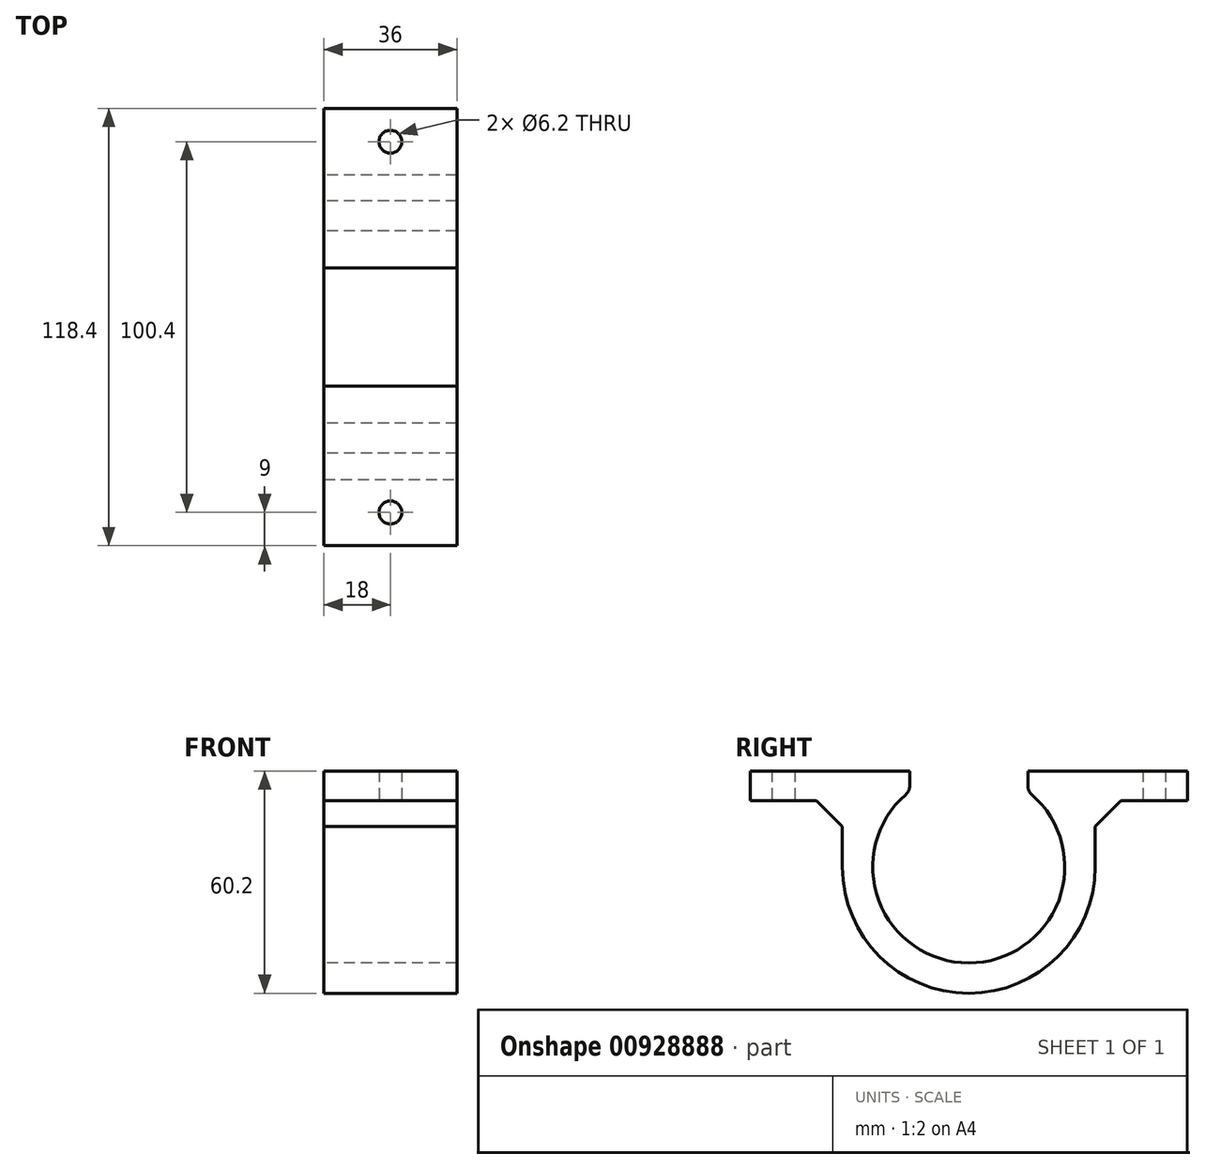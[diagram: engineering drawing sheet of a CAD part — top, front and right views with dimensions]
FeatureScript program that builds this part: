
annotation { "Feature Type Name" : "Feature", "Feature Type Description" : "" }
export const myFeature = defineFeature(function(context is Context, id is Id, definition is map)
    precondition{}
    {
        {
            var Q0;
            Q0=qCreatedBy(makeId("Right.planeOp"),FACE);
            var sketch = newSketch(context, id + "F0", { "sketchPlane" : qUnion([Q0])});
            skCircle(sketch, "E0", {"center": v(0, 0) * mm, "radius": 26 * mm, "construction": true});
            skLineSegment(sketch, "E1", {"start": v(26, 0) * mm, "end": v(26, 26) * mm, "construction": true});
            skLineSegment(sketch, "E2", {"start": v(26, 26) * mm, "end": v(-26, 26) * mm, "construction": true});
            skLineSegment(sketch, "E3", {"start": v(-26, 26) * mm, "end": v(-26, 0) * mm, "construction": true});
            skLineSegment(sketch, "E4", {"start": v(-26, 0) * mm, "end": v(26, 0) * mm, "construction": true});
            skLineSegment(sketch, "E5", {"start": v(-26, 26) * mm, "end": v(-59.2, 26) * mm});
            skLineSegment(sketch, "E6", {"start": v(-59.2, 26) * mm, "end": v(-59.2, 18) * mm});
            skLineSegment(sketch, "E7", {"start": v(-59.2, 18) * mm, "end": v(-34.2, 18) * mm});
            skLineSegment(sketch, "E8", {"start": v(-34.2, 18) * mm, "end": v(-34.2, 0) * mm});
            skLineSegment(sketch, "E9", {"start": v(26, 26) * mm, "end": v(59.2, 26) * mm});
            skLineSegment(sketch, "E10", {"start": v(59.2, 26) * mm, "end": v(59.2, 18) * mm});
            skLineSegment(sketch, "E11", {"start": v(59.2, 18) * mm, "end": v(34.2, 18) * mm});
            skLineSegment(sketch, "E12", {"start": v(34.2, 18) * mm, "end": v(34.2, 0) * mm});
            skArc(sketch, "E13", {"start": v(-34.2, 0) * mm, "mid": v(0, -34.2) * mm, "end": v(34.2, 0) * mm});
            skArc(sketch, "E14", {"start": v(-26, 0) * mm, "mid": v(0, -26) * mm, "end": v(26, 0) * mm});
            skLineSegment(sketch, "E15", {"start": v(-46.7, 18) * mm, "end": v(-46.7, 26) * mm, "construction": true});
            skLineSegment(sketch, "E16", {"start": v(46.7, 18) * mm, "end": v(46.7, 26) * mm, "construction": true});
            skLineSegment(sketch, "E17", {"start": v(34.2, 18) * mm, "end": v(34.2, 26) * mm, "construction": true});
            skLineSegment(sketch, "E18", {"start": v(-34.2, 18) * mm, "end": v(-34.2, 26) * mm, "construction": true});
            skArc(sketch, "E19", {"start": v(26, 0) * mm, "mid": v(23.37, 11.4) * mm, "end": v(16, 20.5) * mm});
            skLineSegment(sketch, "E20", {"start": v(26, 26) * mm, "end": v(16, 26) * mm});
            skLineSegment(sketch, "E21", {"start": v(16, 26) * mm, "end": v(16, 20.5) * mm});
            skArc(sketch, "E22", {"start": v(-26, 0) * mm, "mid": v(-23.37, 11.4) * mm, "end": v(-16, 20.5) * mm});
            skLineSegment(sketch, "E23", {"start": v(16, 20.5) * mm, "end": v(-16, 20.5) * mm, "construction": true});
            skLineSegment(sketch, "E24", {"start": v(-16, 20.5) * mm, "end": v(-16, 26) * mm});
            skLineSegment(sketch, "E25", {"start": v(-16, 26) * mm, "end": v(-26, 26) * mm});
            skSolve(sketch);
        }
        {
            var Q0;
            Q0=makeQuery(id+"F0.imprint","IMPRINT",FACE,{"disambiguationData":[TD([[makeQuery(id+"F0.imprint","IMPRINT",EDGE,{"derivedFrom":sQuery(id+"F0.wireOp",EDGE,"E5")}),1.0]])]});
            extrude(context, id + "F1", {"entities" : qUnion([Q0]), "depth" : 36 * mm, "offsetDistance" : 25 * mm});
        }
        {
            var Q0;
            Q0=makeQuery(id+"F1.opExtrude","SWEPT_FACE",FACE,{"disambiguationData":[OSD([sQuery(id+"F0.wireOp",EDGE,"E7")])]});
            var sketch = newSketch(context, id + "F2", { "sketchPlane" : qUnion([Q0])});
            skLineSegment(sketch, "E26", {"start": v(36, 50.2) * mm, "end": v(0, 50.2) * mm, "construction": true});
            skCircle(sketch, "E27", {"center": v(18, 50.2) * mm, "radius": 3.1 * mm});
            skLineSegment(sketch, "E28", {"start": v(36, -50.2) * mm, "end": v(0, -50.2) * mm, "construction": true});
            skCircle(sketch, "E29", {"center": v(18, -50.2) * mm, "radius": 3.1 * mm});
            skCircle(sketch, "E30", {"center": v(18, 50.2) * mm, "radius": 9 * mm, "construction": true});
            skCircle(sketch, "E31", {"center": v(18, -50.2) * mm, "radius": 9 * mm, "construction": true});
            skSolve(sketch);
        }
        {
            var Q0;
            Q0=qSketchRegion(id+"F2",true);
            extrude(context, id + "F3", {"entities" : qUnion([Q0]), "operationType" : NewBodyOperationType.REMOVE, "endBound" : BoundingType.THROUGH_ALL, "oppositeDirection" : true, "depth" : 25 * mm, "offsetDistance" : 25 * mm});
        }
        {
            var Q0;
            Q0=makeQuery(id+"F1.opExtrude","SWEPT_EDGE",EDGE,{"disambiguationData":[OSD([sQuery(id+"F0.wireOp",EDGE,"E7"),sQuery(id+"F0.wireOp",EDGE,"E8")])]});
            var Q1;
            Q1=makeQuery(id+"F1.opExtrude","SWEPT_EDGE",EDGE,{"disambiguationData":[OSD([sQuery(id+"F0.wireOp",EDGE,"E11"),sQuery(id+"F0.wireOp",EDGE,"E12")])]});
            chamfer(context, id + "F4", {"entities" : qUnion([Q0, Q1]), "width" : 7 * mm, "tangentPropagation" : true});
        }
        {
            var Q0;
            Q0=makeQuery(id+"F1.opExtrude","SWEPT_EDGE",EDGE,{"disambiguationData":[OSD([sQuery(id+"F0.wireOp",EDGE,"E19"),sQuery(id+"F0.wireOp",EDGE,"E21")])]});
            var Q1;
            Q1=makeQuery(id+"F1.opExtrude","SWEPT_EDGE",EDGE,{"disambiguationData":[OSD([sQuery(id+"F0.wireOp",EDGE,"E22"),sQuery(id+"F0.wireOp",EDGE,"E24")])]});
            fillet(context, id + "F5", {"entities" : qUnion([Q0, Q1]), "radius" : 3 * mm, "tangentPropagation" : true, "allowEdgeOverflow" : false});
        }
    });
